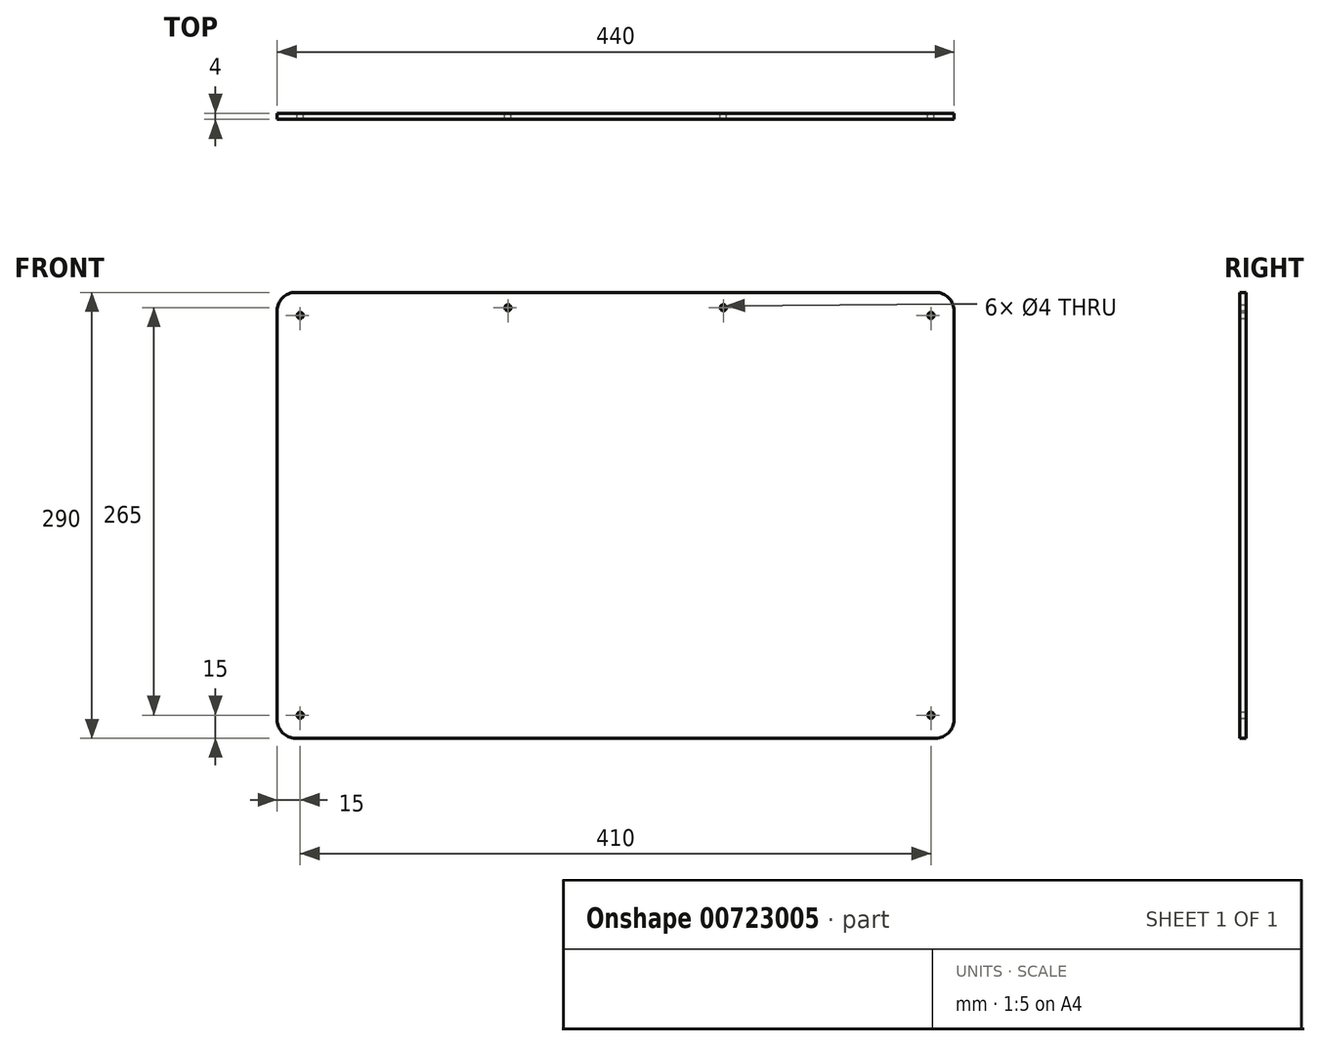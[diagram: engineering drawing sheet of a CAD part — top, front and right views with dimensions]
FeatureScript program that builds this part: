
annotation { "Feature Type Name" : "Feature", "Feature Type Description" : "" }
export const myFeature = defineFeature(function(context is Context, id is Id, definition is map)
    precondition{}
    {
        {
            var Q0;
            Q0=qCreatedBy(makeId("Front.planeOp"),FACE);
            var sketch = newSketch(context, id + "F0", { "sketchPlane" : qUnion([Q0])});
            skLineSegment(sketch, "E0.bottom", {"start": v(0, 0) * mm, "end": v(440, 0) * mm});
            skLineSegment(sketch, "E0.top", {"start": v(0, 290) * mm, "end": v(440, 290) * mm});
            skLineSegment(sketch, "E0.left", {"start": v(0, 0) * mm, "end": v(0, 290) * mm});
            skLineSegment(sketch, "E0.right", {"start": v(440, 0) * mm, "end": v(440, 290) * mm});
            skLineSegment(sketch, "E1.bottom", {"start": v(55, 270) * mm, "end": v(385, 270) * mm, "construction": true});
            skLineSegment(sketch, "E1.top", {"start": v(55, 20) * mm, "end": v(385, 20) * mm, "construction": true});
            skLineSegment(sketch, "E1.left", {"start": v(55, 270) * mm, "end": v(55, 20) * mm, "construction": true});
            skLineSegment(sketch, "E1.right", {"start": v(385, 270) * mm, "end": v(385, 20) * mm, "construction": true});
            skCircle(sketch, "E2", {"center": v(15, 15) * mm, "radius": 2 * mm});
            skCircle(sketch, "E3", {"center": v(425, 15) * mm, "radius": 2 * mm});
            skCircle(sketch, "E4", {"center": v(425, 275) * mm, "radius": 2 * mm});
            skCircle(sketch, "E5", {"center": v(15, 275) * mm, "radius": 2 * mm});
            skCircle(sketch, "E6", {"center": v(150, 280) * mm, "radius": 2 * mm});
            skCircle(sketch, "E7", {"center": v(290, 280) * mm, "radius": 2 * mm});
            skSolve(sketch);
        }
        {
            var Q0;
            Q0 = qSketchRegion(id + "F0", true);
            extrude(context, id + "F1", {"entities" : qUnion([Q0]), "depth" : 4 * mm, "offsetDistance" : 25 * mm});
        }
        {
            var Q0;
            Q0=makeQuery(id+"F1.opExtrude","SWEPT_EDGE",EDGE,{"disambiguationData":[OSD([sQuery(id+"F0.wireOp",EDGE,"E0.top"),sQuery(id+"F0.wireOp",EDGE,"E0.right")])]});
            var Q1;
            Q1=makeQuery(id+"F1.opExtrude","SWEPT_EDGE",EDGE,{"disambiguationData":[OSD([sQuery(id+"F0.wireOp",EDGE,"E0.top"),sQuery(id+"F0.wireOp",EDGE,"E0.left")])]});
            var Q2;
            Q2=makeQuery(id+"F1.opExtrude","SWEPT_EDGE",EDGE,{"disambiguationData":[OSD([sQuery(id+"F0.wireOp",EDGE,"E0.bottom"),sQuery(id+"F0.wireOp",EDGE,"E0.left")])]});
            var Q3;
            Q3=makeQuery(id+"F1.opExtrude","SWEPT_EDGE",EDGE,{"disambiguationData":[OSD([sQuery(id+"F0.wireOp",EDGE,"E0.bottom"),sQuery(id+"F0.wireOp",EDGE,"E0.right")])]});
            fillet(context, id + "F2", {"entities" : qUnion([Q0, Q1, Q2, Q3]), "radius" : 12 * mm, "tangentPropagation" : true, "allowEdgeOverflow" : false});
        }
    });
